# Revit family: QF_Summit_CCE227SS_2_Burner Coil Cooktop
name_source: partatom
category: Specialty Equipment
units: mm (PartAtom-declared; Revit-internal decimal feet)

## family parameters
Always vertical = Yes
Cut with Voids When Loaded = No
Part Type = Normal
Room Calculation Point = No
Round Connector Dimension = Use Diameter
Shared = No
Work Plane-Based = No

## types (1)
- QF_Summit_CCE227SS_2_Burner Coil Cooktop
    Apparent Power = 1610 VA
    Conn Conduit = Yes
    Cycle = 60 Hz
    Default Elevation = 0"
    Depth = 19 3/4"
    Description = 2 Burner Coil Cooktop
    Elec Conn Connection Height = 0"
    Elec Conn RI Height = 0"
    FL Amps = 7 A
    Foodservice Equipment Identifier = Yes
    Height = 3 1/4"
    Identify Quantity as Lot = Yes
    Length = 12"
    Manufacturer = Summit
    Max Overcurrent Protection = 0 A
    Min Ckt Ampacity = 0 A
    Model = CCE227SS
    Number of Poles = 1
    Phase = 1
    Volts = 230 V
    Watts = 1610 W
    Weight in Pounds = 14

## geometry (parser evidence)
native form markers: Sweep x6
no freeform markers — native parametric forms only
